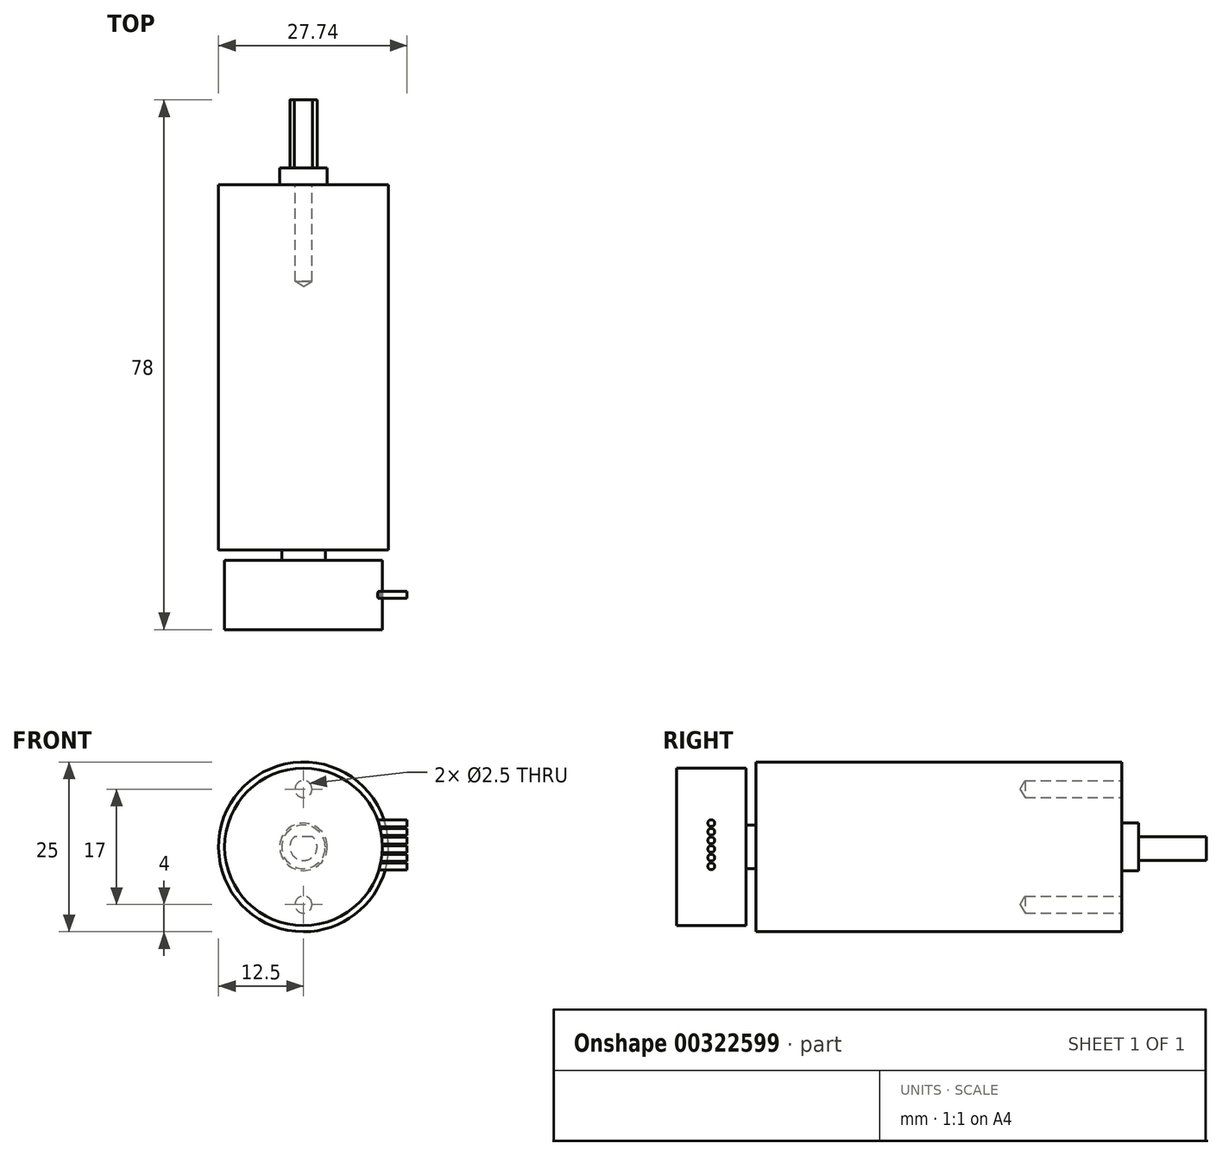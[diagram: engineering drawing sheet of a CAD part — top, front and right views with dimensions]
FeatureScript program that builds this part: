
annotation { "Feature Type Name" : "Feature", "Feature Type Description" : "" }
export const myFeature = defineFeature(function(context is Context, id is Id, definition is map)
    precondition{}
    {
        {
            var Q0;
            Q0=qCreatedBy(makeId("Front.planeOp"),FACE);
            var sketch = newSketch(context, id + "F0", { "sketchPlane" : qUnion([Q0])});
            skCircle(sketch, "E0", {"center": v(0, 0) * mm, "radius": 12.5 * mm});
            skSolve(sketch);
        }
        {
            var Q0;
            Q0=makeQuery(id+"F0.imprint","IMPRINT",FACE,{"disambiguationData":[TD([[makeQuery(id+"F0.imprint","IMPRINT",EDGE,{"derivedFrom":sQuery(id+"F0.wireOp",EDGE,"E0")}),1.0]])]});
            extrude(context, id + "F1", {"entities" : qUnion([Q0]), "oppositeDirection" : true, "depth" : 30.8 * mm + 23 * mm});
        }
        {
            var Q0;
            Q0=makeQuery(id+"F1.opExtrude","CAP_FACE",FACE,{"disambiguationData":[OSD([sQuery(id+"F0.wireOp",EDGE,"E0")])],"isStart":false});
            var sketch = newSketch(context, id + "F2", { "sketchPlane" : qUnion([Q0])});
            skCircle(sketch, "E1", {"center": v(0, 0) * mm, "radius": 3.5 * mm});
            skSolve(sketch);
        }
        {
            var Q0;
            Q0=makeQuery(id+"F2.imprint","IMPRINT",FACE,{"disambiguationData":[TD([[makeQuery(id+"F2.imprint","IMPRINT",EDGE,{"derivedFrom":sQuery(id+"F2.wireOp",EDGE,"E1")}),1.0]])]});
            extrude(context, id + "F3", {"entities" : qUnion([Q0]), "operationType" : NewBodyOperationType.ADD, "depth" : 2.5 * mm});
        }
        {
            var Q0;
            Q0=makeQuery(id+"F3.opExtrude","CAP_FACE",FACE,{"disambiguationData":[OSD([sQuery(id+"F2.wireOp",EDGE,"E1")])],"isStart":false});
            var sketch = newSketch(context, id + "F4", { "sketchPlane" : qUnion([Q0])});
            skArc(sketch, "E2", {"start": v(-1.32, 1.5) * mm, "mid": v(0, -2) * mm, "end": v(1.32, 1.5) * mm});
            skLineSegment(sketch, "E3", {"start": v(-1.32, 1.5) * mm, "end": v(1.32, 1.5) * mm});
            skSolve(sketch);
        }
        {
            var Q0;
            Q0 = qSketchRegion(id + "F4", true);
            extrude(context, id + "F5", {"entities" : qUnion([Q0]), "operationType" : NewBodyOperationType.ADD, "depth" : 10 * mm});
        }
        {
            var Q0;
            Q0=makeQuery(id+"F1.opExtrude","CAP_FACE",FACE,{"disambiguationData":[OSD([sQuery(id+"F0.wireOp",EDGE,"E0")])],"isStart":true});
            var sketch = newSketch(context, id + "F6", { "sketchPlane" : qUnion([Q0])});
            skCircle(sketch, "E4", {"center": v(0, 0) * mm, "radius": 3.2 * mm});
            skSolve(sketch);
        }
        {
            var Q0;
            Q0=makeQuery(id+"F6.imprint","IMPRINT",FACE,{"disambiguationData":[TD([[makeQuery(id+"F6.imprint","IMPRINT",EDGE,{"derivedFrom":sQuery(id+"F6.wireOp",EDGE,"E4")}),1.0]])]});
            extrude(context, id + "F7", {"entities" : qUnion([Q0]), "operationType" : NewBodyOperationType.ADD, "depth" : 1.5 * mm});
        }
        {
            var Q0;
            Q0=makeQuery(id+"F7.opExtrude","CAP_FACE",FACE,{"disambiguationData":[OSD([sQuery(id+"F6.wireOp",EDGE,"E4")])],"isStart":false});
            var sketch = newSketch(context, id + "F8", { "sketchPlane" : qUnion([Q0])});
            skCircle(sketch, "E5", {"center": v(0, 0) * mm, "radius": 11.6 * mm});
            skSolve(sketch);
        }
        {
            var Q0;
            Q0=makeQuery(id+"F8.imprint","IMPRINT",FACE,{"disambiguationData":[TD([[makeQuery(id+"F8.imprint","IMPRINT",EDGE,{"derivedFrom":sQuery(id+"F8.wireOp",EDGE,"E5")}),1.0]])]});
            var Q1;
            Q1=makeQuery(id+"F8.imprint","IMPRINT",FACE,{"disambiguationData":[TD([[makeQuery(id+"F8.imprint","IMPRINT",EDGE,{"derivedFrom":makeQuery(id+"F7.opExtrude","CAP_EDGE",EDGE,{"disambiguationData":[OSD([sQuery(id+"F6.wireOp",EDGE,"E4")])],"isStart":false})}),1.0]])]});
            extrude(context, id + "F9", {"entities" : qUnion([Q0, Q1]), "operationType" : NewBodyOperationType.ADD, "depth" : 11.7 * mm - 1.5 * mm});
        }
        {
            var Q0;
            Q0=makeQuery(id+"F1.opExtrude","CAP_FACE",FACE,{"disambiguationData":[OSD([sQuery(id+"F0.wireOp",EDGE,"E0")])],"isStart":false});
            var sketch = newSketch(context, id + "F10", { "sketchPlane" : qUnion([Q0])});
            skPoint(sketch, "E6", {"position": v(0, 8.5) * mm});
            skPoint(sketch, "E7", {"position": v(0, -8.5) * mm});
            skPoint(sketch, "E8", {"position": v(0, 0) * mm});
            skLineSegment(sketch, "E9", {"start": v(0, 8.5) * mm, "end": v(0, -8.5) * mm, "construction": true});
            skLineSegment(sketch, "E10", {"start": v(0, 0) * mm, "end": v(0, 0) * mm});
            skSolve(sketch);
        }
        {
            var Q0;
            Q0=sQuery(id+"F10.wireOp",VERTEX,"E6");
            var Q1;
            Q1=sQuery(id+"F10.wireOp",VERTEX,"E7");
            var Q2;
            Q2=makeQuery(id+"F1.opExtrude","SWEPT_BODY",BODY,{"disambiguationData":[OSD([sQuery(id+"F0.wireOp",EDGE,"E0")])]});
            hole(context, id + "F11", {"style" : HoleStyle.SIMPLE, "endStyle" : HoleEndStyle.BLIND, "standardTappedOrClearance" : lookupTablePath({ "standard" : "ISO", "engagement" : "75%", "pitch" : "0.5 mm", "size" : "M3", "type" : "Tapped" }), "standardBlindInLast" : lookupTablePath({ "standard" : "ISO", "engagement" : "75%", "pitch" : "0.5 mm", "size" : "M3", "type" : "Tapped" }), "holeDiameter" : 2.5 * mm, "showTappedDepth" : true, "holeDepth" : 14.2 * mm, "isTappedThrough" : true, "tappedDepth" : 12.7 * mm, "tapClearance" : 3, "locations" : qUnion([Q0, Q1]), "scope" : qUnion([Q2]), "majorDiameter" : 3 * mm});
        }
        {
            var Q0;
            Q0=qCreatedBy(makeId("Right.planeOp"),FACE);
            cPlane(context, id + "F12", {"entities" : qUnion([Q0]), "cplaneType" : CPlaneType.OFFSET, "offset" : 15.24 * mm, "width" : 152.4 * mm, "height" : 152.4 * mm});
        }
        {
            var Q0;
            Q0=qCreatedBy(id+"F12.planeOp",FACE);
            var sketch = newSketch(context, id + "F13", { "sketchPlane" : qUnion([Q0])});
            skCircle(sketch, "E11", {"center": v(-6.6, -2.86) * mm, "radius": 0.5 * mm});
            skCircle(sketch, "E12", {"center": v(-6.6, -1.59) * mm, "radius": 0.5 * mm});
            skCircle(sketch, "E13", {"center": v(-6.6, -0.32) * mm, "radius": 0.5 * mm});
            skCircle(sketch, "E14", {"center": v(-6.6, 0.95) * mm, "radius": 0.5 * mm});
            skCircle(sketch, "E15", {"center": v(-6.6, 2.22) * mm, "radius": 0.5 * mm});
            skCircle(sketch, "E16", {"center": v(-6.6, 3.5) * mm, "radius": 0.5 * mm});
            skLineSegment(sketch, "E17", {"start": v(-6.6, 3.5) * mm, "end": v(-6.6, 2.22) * mm, "construction": true});
            skLineSegment(sketch, "E18", {"start": v(-6.6, 0.95) * mm, "end": v(-6.6, 2.22) * mm, "construction": true});
            skLineSegment(sketch, "E19", {"start": v(-6.6, -0.32) * mm, "end": v(-6.6, 0.95) * mm, "construction": true});
            skLineSegment(sketch, "E20", {"start": v(-6.6, -1.59) * mm, "end": v(-6.6, -0.32) * mm, "construction": true});
            skLineSegment(sketch, "E21", {"start": v(-6.6, -2.86) * mm, "end": v(-6.6, -1.59) * mm, "construction": true});
            skLineSegment(sketch, "E22", {"start": v(0, 0) * mm, "end": v(-6.6, 0) * mm, "construction": true});
            skSolve(sketch);
        }
        {
            var Q0;
            Q0 = qSketchRegion(id + "F13", true);
            var Q1;
            Q1=makeQuery(id+"F9.opExtrude","SWEPT_FACE",FACE,{"disambiguationData":[OSD([sQuery(id+"F8.wireOp",EDGE,"E5")])]});
            extrude(context, id + "F14", {"entities" : qUnion([Q0]), "endBound" : BoundingType.UP_TO_SURFACE, "oppositeDirection" : true, "endBoundEntityFace" : qUnion([Q1]), "depth" : 25.4 * mm});
        }
    });
